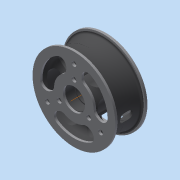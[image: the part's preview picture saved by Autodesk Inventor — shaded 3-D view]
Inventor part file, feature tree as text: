
AUTODESK INVENTOR PART (.ipt)
format: ipt  version: 2015 (Build 190159000, 159)  size: 1,552,384 bytes
history: native  units: in
note: dims shown in document units (in); Inventor stores cm internally (conversion verified against a paired STEP export)
features: extrude x12, sketch x12, fillet x11, projected_geometry x5, pattern_circular x4, chamfer x3, plane x3, mirror x3, revolve x2, split x1, other x1
ambient origin geometry x8: Origin, YZ Plane, XZ Plane, XY Plane, X Axis, Y Axis, Z Axis, Center Point
bodies: Solid3 (feature_tree), Solid11 (feature_tree), Solid14 (feature_tree), Solid12 (feature_tree), Solid13 (feature_tree)
feature tree (57):
  revolve  "Revolution3"  [1 undecoded]
  revolve  "Revolution4"  [1 undecoded]
  extrude  "Extrusion16"  Depth=0.437in
  extrude  "Extrusion19"  Depth=0.75in
  pattern_circular  "Circular Pattern9"  Count=3 Angle=360.0deg
  sketch  "Sketch19"  dims[d0=1.5625in d1=1.125in]
  chamfer  "Chamfer3"  Distance=0.625in
  extrude  "Extrusion17"  Depth=0.625in TaperAngle=0.0deg
  extrude  "Extrusion18"  Depth=0.0938in
  fillet  "Fillet14"  Radius=1.1811in
  pattern_circular  "Circular Pattern10"  [2 undecoded]
  plane  "Work Plane8"
  plane  "Work Plane9"
  extrude  "Extrusion25"  Depth=0.625in TaperAngle=0.0deg
  pattern_circular  "Circular Pattern12"  [2 undecoded]
  plane  "Work Plane5"
  extrude  "Extrusion26"  Depth=0.9055in
  fillet  "Fillet22"  Radius=0.0938in
  chamfer  "Chamfer4"  Distance=1.625in
  fillet  "Fillet28"  Radius=0.0938in
  fillet  "Fillet29"  Radius=0.625in
  chamfer  "Chamfer5"  Distance=0.0938in
  fillet  "Fillet30"  Radius=0.0938in
  fillet  "Fillet31"  Radius=0.25in
  extrude  "Extrusion27"  Depth=1.1811in TaperAngle=360.0deg
  extrude  "Extrusion28"  Depth=0.0618in
  fillet  "Fillet33"  Radius=0.0618in
  fillet  "Fillet32"  Radius=0.125in
  split  "Split1"
  extrude  "Extrusion21"  Depth=1.1811in TaperAngle=360.0deg
  extrude  "Extrusion22"  Depth=2.75in
  extrude  "Extrusion23"  Depth=0.125in TaperAngle=45.0deg
  extrude  "Extrusion24"  [1 undecoded]
  fillet  "Fillet17"  [1 undecoded]
  pattern_circular  "Circular Pattern11"  [2 undecoded]
  mirror  "Mirror5"
  fillet  "Fillet26"  Radius=1.0in
  fillet  "Fillet27"  Radius=0.1562in
  mirror  "Mirror6"
  mirror  "Mirror7"
  projected_geometry  "Projected Loop16"
  sketch  "Sketch20"  dims[d2=0.437in d4=0.3937in]
  sketch  "Sketch21"  dims[d5=0.3937in d6=0.437in]
  projected_geometry  "Projected Loop17"
  sketch  "Sketch22"  dims[d13=2.0in d14=0.75in]
  sketch  "Sketch24"  dims[d15=0.25in]
  sketch  "Sketch25"  dims[d37=90.0deg]
  sketch  "Sketch26"  dims[d126=90.0deg]
  sketch  "Sketch27"  dims[d127=0.196in]
  sketch  "Sketch28"  dims[d128=0.6955in]
  projected_geometry  "Projected Loop22"
  other  "Pattern of Solid11:3"
  sketch  "Sketch29"  dims[d129=0.625in d130=0.0in d131=1.1811in d132=360.0deg]
  sketch  "Sketch30"  dims[d134=0.25in d135=0.625in d136=0.0in]
  projected_geometry  "Projected Loop23"
  sketch  "Sketch31"  dims[d137=0.196in d138=0.625in d139=0.0in d140=0.0938in d141=1.1811in d142=360.0deg d144=0.25in d145=0.625in d146=0.0in d155=3.375in d156=0.9055in d157=0.0938in d158=0.0in d159=1.625in d161=0.0938in d162=0.0in d163=0.625in d164=0.0938in d165=0.0in d166=0.0938in d167=0.0in d168=0.25in d169=1.1811in d170=360.0deg d172=0.0618in d173=0.0618in d174=0.125in d175=0.0in d179=1.1811in d180=360.0deg d184=2.75in d185=0.125in d186=0.125in d187=45.0deg d191=-0.3125in d192=-0.3125in d193=0.375in d194=1.0in d195=0.0in d196=0.1562in d197=0.5in d201=0.125in d202=0.125in d203=0.125in d204=0.125in d205=45.0deg d206=0.125in d207=0.375in d208=0.125in d209=0.125in d210=45.0deg d211=0.375in d212=0.375in d213=0.25in d215=0.0312in d216=0.0in d217=0.0312in d218=0.0in d219=0.0625in d220=0.0625in d221=0.0625in]
  projected_geometry  "Projected Loop24"
note: 10 required parameter values undecoded (feature->parameter linkage not recoverable at this tier; creation-order binding heuristic only, values carry confidence <= 0.55)